# Revit family: Sanitary-Showers_DURAVIT-AG_Showers-Accessoires-Shower-hose-Bronze-Brushed-UV0610007_NEW
name_source: partatom
category: Plumbing Fixtures
units: mm (PartAtom-declared; Revit-internal decimal feet)

## family parameters
Cut with Voids When Loaded = No
Host = Face
OmniClass Number = 23.31.17.00
OmniClass Title = Showers
Part Type = Normal
Room Calculation Point = No
Round Connector Dimension = Use Diameter
Shared = No

## types (5) — shared parameters
Date Updated = 2025/07/23
Default Elevation = 1219 mm
Depth = 23 mm  [stored 0.0754593 ft]
Description = Duravit Showers & Accessories Shower hose Bronze Brushed Rotation lock: Yes Nut shape: Conical 1600 mm - UV0610007004
Height = 1600 mm  [stored 5.24934 ft]
Installation instructions = https://duravit-public-assets.s3.eu-central-1.amazonaws.com
Manufacturer = Duravit
Model = Shower hose - UV0610007
Product Documentation Link = https://pro.duravit.com
Product Page URL = https://pro.duravit.com
Product data url = https://bimobject.com
URL = https://www.duravit.com
Version = 2
Weight = 0.35 kg
Width = 23 mm  [stored 0.0754593 ft]

## per-type parameters (varying)
| type | Article Number | Material 1 |
| 10 - Chrome | UV0610007010 | Duravit - Metal - 10 - Chrome |
| 46 - Black Matt | UV0610007046 | Duravit - Metal - 46 - Black Matt |
| 04 - Brushed Bronze | UV0610007004 | Duravit - Metal - 04 - Brushed Bronze |
| 34 - Polished Gold | UV0610007034 | Duravit - Metal - 34 - Polished Gold |
| 70 - Brushed Stainless Steel | UV0610007070 | Duravit - Metal - 70 - Brushed Stainless Steel |

note: [stored X ft] marks values corroborated as IEEE doubles in the binary element streams (Revit-internal decimal feet)

## geometry (parser evidence)
native form markers: Sweep x3
no freeform markers — native parametric forms only
